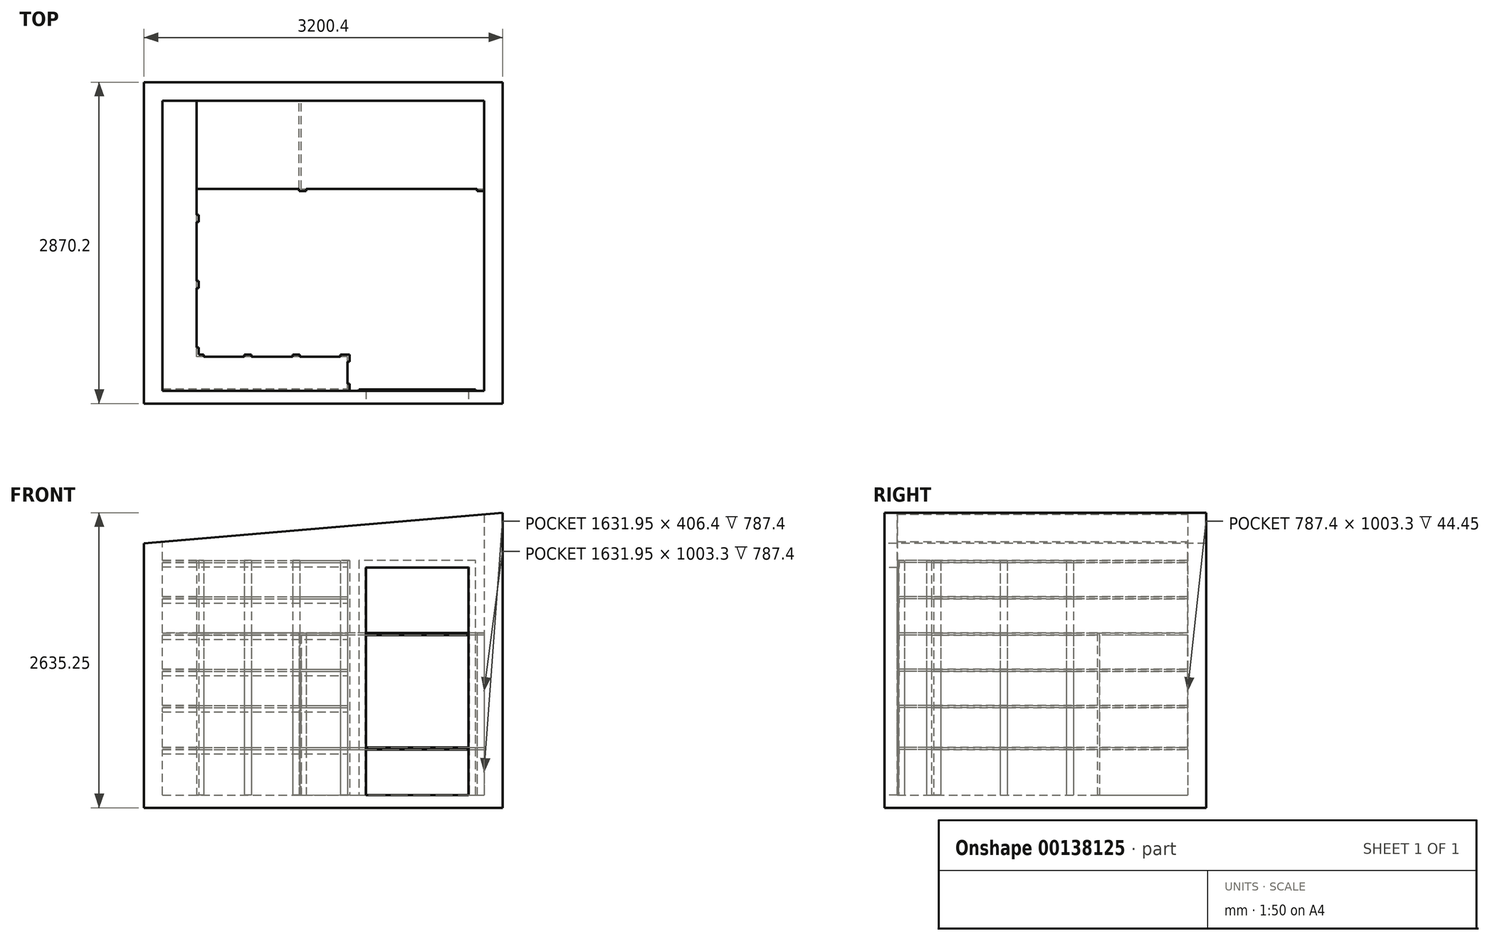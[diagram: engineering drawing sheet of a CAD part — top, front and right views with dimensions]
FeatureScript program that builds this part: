
annotation { "Feature Type Name" : "Feature", "Feature Type Description" : "" }
export const myFeature = defineFeature(function(context is Context, id is Id, definition is map)
    precondition{}
    {
        {
            var Q0;
            Q0=qCreatedBy(makeId("Right.planeOp"),FACE);
            var sketch = newSketch(context, id + "F0", { "sketchPlane" : qUnion([Q0])});
            skLineSegment(sketch, "E0.bottom", {"start": v(0, 0) * mm, "end": v(2590.8, 0) * mm});
            skLineSegment(sketch, "E0.top", {"start": v(0, 2520.95) * mm, "end": v(2590.8, 2520.95) * mm});
            skLineSegment(sketch, "E0.left", {"start": v(0, 0) * mm, "end": v(0, 2520.95) * mm});
            skLineSegment(sketch, "E0.right", {"start": v(2590.8, 0) * mm, "end": v(2590.8, 2520.95) * mm});
            skSolve(sketch);
        }
        {
            var Q0;
            Q0 = qSketchRegion(id + "F0", true);
            extrude(context, id + "F1", {"entities" : qUnion([Q0]), "depth" : 165.1 * mm});
        }
        {
            var Q0;
            Q0=makeQuery(id+"F1.opExtrude","SWEPT_FACE",FACE,{"disambiguationData":[OSD([sQuery(id+"F0.wireOp",EDGE,"E0.left")])]});
            var sketch = newSketch(context, id + "F2", { "sketchPlane" : qUnion([Q0])});
            skLineSegment(sketch, "E1.bottom", {"start": v(0, 2520.95) * mm, "end": v(3035.3, 2520.95) * mm});
            skLineSegment(sketch, "E1.top", {"start": v(0, 0) * mm, "end": v(3035.3, 0) * mm});
            skLineSegment(sketch, "E1.left", {"start": v(0, 2520.95) * mm, "end": v(0, 0) * mm});
            skLineSegment(sketch, "E1.right", {"start": v(3035.3, 2520.95) * mm, "end": v(3035.3, 0) * mm});
            skSolve(sketch);
        }
        {
            var Q0;
            Q0 = qSketchRegion(id + "F2", true);
            extrude(context, id + "F3", {"entities" : qUnion([Q0]), "operationType" : NewBodyOperationType.ADD, "depth" : 114.3 * mm});
        }
        {
            var Q0;
            Q0=makeQuery(id+"F1.opExtrude","SWEPT_FACE",FACE,{"disambiguationData":[OSD([sQuery(id+"F0.wireOp",EDGE,"E0.right")])]});
            var sketch = newSketch(context, id + "F4", { "sketchPlane" : qUnion([Q0])});
            skLineSegment(sketch, "E2.bottom", {"start": v(0, 2520.95) * mm, "end": v(-3035.3, 2520.95) * mm});
            skLineSegment(sketch, "E2.top", {"start": v(0, 0) * mm, "end": v(-3035.3, 0) * mm});
            skLineSegment(sketch, "E2.left", {"start": v(0, 2520.95) * mm, "end": v(0, 0) * mm});
            skLineSegment(sketch, "E2.right", {"start": v(-3035.3, 2520.95) * mm, "end": v(-3035.3, 0) * mm});
            skSolve(sketch);
        }
        {
            var Q0;
            Q0 = qSketchRegion(id + "F4", true);
            extrude(context, id + "F5", {"entities" : qUnion([Q0]), "operationType" : NewBodyOperationType.ADD, "depth" : 165.1 * mm});
        }
        {
            var Q0;
            Q0=makeQuery(id+"F3.opExtrude","SWEPT_FACE",FACE,{"disambiguationData":[OSD([sQuery(id+"F2.wireOp",EDGE,"E1.right")])]});
            var sketch = newSketch(context, id + "F6", { "sketchPlane" : qUnion([Q0])});
            skLineSegment(sketch, "E3.bottom", {"start": v(-114.3, 2520.95) * mm, "end": v(2755.9, 2520.95) * mm});
            skLineSegment(sketch, "E3.top", {"start": v(-114.3, 0) * mm, "end": v(2755.9, 0) * mm});
            skLineSegment(sketch, "E3.left", {"start": v(-114.3, 2520.95) * mm, "end": v(-114.3, 0) * mm});
            skLineSegment(sketch, "E3.right", {"start": v(2755.9, 2520.95) * mm, "end": v(2755.9, 0) * mm});
            skSolve(sketch);
        }
        {
            var Q0;
            Q0 = qSketchRegion(id + "F6", true);
            extrude(context, id + "F7", {"entities" : qUnion([Q0]), "operationType" : NewBodyOperationType.ADD, "depth" : 165.1 * mm});
        }
        {
            var Q0;
            Q0=makeQuery(id+"F7.boolean.opBoolean","MERGE",FACE,{"derivedFrom":[makeQuery(id+"F3.opExtrude","CAP_FACE",FACE,{"disambiguationData":[OSD([sQuery(id+"F2.wireOp",EDGE,"E1.bottom"),sQuery(id+"F2.wireOp",EDGE,"E1.top"),sQuery(id+"F2.wireOp",EDGE,"E1.left"),sQuery(id+"F2.wireOp",EDGE,"E1.right")])],"isStart":false}),makeQuery(id+"F7.opExtrude","SWEPT_FACE",FACE,{"disambiguationData":[OSD([sQuery(id+"F6.wireOp",EDGE,"E3.left")])]})]});
            var sketch = newSketch(context, id + "F8", { "sketchPlane" : qUnion([Q0])});
            skLineSegment(sketch, "E4.bottom", {"start": v(2895.6, 0) * mm, "end": v(1981.2, 0) * mm});
            skLineSegment(sketch, "E4.top", {"start": v(2895.6, 2032) * mm, "end": v(1981.2, 2032) * mm});
            skLineSegment(sketch, "E4.left", {"start": v(2895.6, 0) * mm, "end": v(2895.6, 2032) * mm});
            skLineSegment(sketch, "E4.right", {"start": v(1981.2, 0) * mm, "end": v(1981.2, 2032) * mm});
            skSolve(sketch);
        }
        {
            var Q0;
            Q0=makeQuery(id+"F8.imprint","IMPRINT",FACE,{"disambiguationData":[TD([[makeQuery(id+"F8.imprint","IMPRINT",EDGE,{"derivedFrom":sQuery(id+"F8.wireOp",EDGE,"E4.top")}),-1.0]])]});
            var sketch = newSketch(context, id + "F9", { "sketchPlane" : qUnion([Q0])});
            skLineSegment(sketch, "E5", {"start": v(0, 2247.9) * mm, "end": v(3200.4, 2520.95) * mm});
            skLineSegment(sketch, "E6", {"start": v(3200.4, 2520.95) * mm, "end": v(0, 2520.95) * mm});
            skLineSegment(sketch, "E7", {"start": v(0, 2520.95) * mm, "end": v(0, 2247.9) * mm});
            skSolve(sketch);
        }
        {
            var Q0;
            Q0 = qSketchRegion(id + "F9", true);
            extrude(context, id + "F10", {"entities" : qUnion([Q0]), "operationType" : NewBodyOperationType.REMOVE, "endBound" : BoundingType.THROUGH_ALL, "oppositeDirection" : true, "depth" : 25.4 * mm});
        }
        {
            var Q0;
            Q0 = qSketchRegion(id + "F8", true);
            extrude(context, id + "F11", {"entities" : qUnion([Q0]), "operationType" : NewBodyOperationType.REMOVE, "oppositeDirection" : true, "depth" : 114.3 * mm});
        }
        {
            var Q0;
            Q0=makeQuery(id+"F7.boolean.opBoolean","MERGE",FACE,{"derivedFrom":[makeQuery(id+"F5.boolean.opBoolean","MERGE",FACE,{"derivedFrom":[makeQuery(id+"F3.boolean.opBoolean","MERGE",FACE,{"derivedFrom":[makeQuery(id+"F1.opExtrude","SWEPT_FACE",FACE,{"disambiguationData":[OSD([sQuery(id+"F0.wireOp",EDGE,"E0.bottom")])]}),makeQuery(id+"F3.opExtrude","SWEPT_FACE",FACE,{"disambiguationData":[OSD([sQuery(id+"F2.wireOp",EDGE,"E1.top")])]})]}),makeQuery(id+"F5.opExtrude","SWEPT_FACE",FACE,{"disambiguationData":[OSD([sQuery(id+"F4.wireOp",EDGE,"E2.top")])]})]}),makeQuery(id+"F7.opExtrude","SWEPT_FACE",FACE,{"disambiguationData":[OSD([sQuery(id+"F6.wireOp",EDGE,"E3.top")])]})]});
            var sketch = newSketch(context, id + "F12", { "sketchPlane" : qUnion([Q0])});
            skLineSegment(sketch, "E8.bottom", {"start": v(0, 114.3) * mm, "end": v(3200.4, 114.3) * mm});
            skLineSegment(sketch, "E8.top", {"start": v(0, -2755.9) * mm, "end": v(3200.4, -2755.9) * mm});
            skLineSegment(sketch, "E8.left", {"start": v(0, 114.3) * mm, "end": v(0, -2755.9) * mm});
            skLineSegment(sketch, "E8.right", {"start": v(3200.4, 114.3) * mm, "end": v(3200.4, -2755.9) * mm});
            skSolve(sketch);
        }
        {
            var Q0;
            Q0 = qSketchRegion(id + "F12", true);
            extrude(context, id + "F13", {"entities" : qUnion([Q0]), "operationType" : NewBodyOperationType.ADD, "depth" : 114.3 * mm});
        }
        {
            var Q0;
            Q0=makeQuery(id+"F3.opExtrude","CAP_FACE",FACE,{"disambiguationData":[OSD([sQuery(id+"F2.wireOp",EDGE,"E1.bottom"),sQuery(id+"F2.wireOp",EDGE,"E1.top"),sQuery(id+"F2.wireOp",EDGE,"E1.left"),sQuery(id+"F2.wireOp",EDGE,"E1.right")])],"isStart":true});
            var sketch = newSketch(context, id + "F14", { "sketchPlane" : qUnion([Q0])});
            skLineSegment(sketch, "E9", {"start": v(-1974.85, 0) * mm, "end": v(-1974.85, 2038.35) * mm});
            skLineSegment(sketch, "E10", {"start": v(-1974.85, 2038.35) * mm, "end": v(-2901.95, 2038.35) * mm});
            skLineSegment(sketch, "E11", {"start": v(-2901.95, 2038.35) * mm, "end": v(-2901.95, 0) * mm});
            skPoint(sketch, "E11.endSnap0", {"position": v(-2965.45, 0) * mm});
            skLineSegment(sketch, "E12", {"start": v(-2901.95, 0) * mm, "end": v(-2959.1, 0) * mm});
            skLineSegment(sketch, "E13", {"start": v(-2959.1, 0) * mm, "end": v(-2959.1, 2095.5) * mm});
            skLineSegment(sketch, "E14", {"start": v(-2959.1, 2095.5) * mm, "end": v(-1917.7, 2095.5) * mm});
            skLineSegment(sketch, "E15", {"start": v(-1917.7, 2095.5) * mm, "end": v(-1917.7, 0) * mm});
            skLineSegment(sketch, "E16", {"start": v(-1917.7, 0) * mm, "end": v(-1974.85, 0) * mm});
            skSolve(sketch);
        }
        {
            var Q0;
            Q0 = qSketchRegion(id + "F14", true);
            extrude(context, id + "F15", {"entities" : qUnion([Q0]), "operationType" : NewBodyOperationType.ADD, "depth" : 12.7 * mm});
        }
        {
            var Q0;
            Q0=makeQuery(id+"F15.boolean.opBoolean","SPLIT",FACE,{"disambiguationData":[TD([makeQuery(id+"F10.boolean.opBoolean","COPY",FACE,{"derivedFrom":makeQuery(id+"F10.opExtrude","SWEPT_FACE",FACE,{"disambiguationData":[OSD([sQuery(id+"F9.wireOp",EDGE,"E5")])]})})])],"derivedFrom":makeQuery(id+"F3.opExtrude","CAP_FACE",FACE,{"disambiguationData":[OSD([sQuery(id+"F2.wireOp",EDGE,"E1.bottom"),sQuery(id+"F2.wireOp",EDGE,"E1.top"),sQuery(id+"F2.wireOp",EDGE,"E1.left"),sQuery(id+"F2.wireOp",EDGE,"E1.right")])],"isStart":true})});
            var Q1;
            Q1=makeQuery(id+"F13.boolean.opBoolean","MERGE",FACE,{"derivedFrom":[makeQuery(id+"F7.boolean.opBoolean","MERGE",FACE,{"derivedFrom":[makeQuery(id+"F3.opExtrude","CAP_FACE",FACE,{"disambiguationData":[OSD([sQuery(id+"F2.wireOp",EDGE,"E1.bottom"),sQuery(id+"F2.wireOp",EDGE,"E1.top"),sQuery(id+"F2.wireOp",EDGE,"E1.left"),sQuery(id+"F2.wireOp",EDGE,"E1.right")])],"isStart":false}),makeQuery(id+"F7.opExtrude","SWEPT_FACE",FACE,{"disambiguationData":[OSD([sQuery(id+"F6.wireOp",EDGE,"E3.left")])]})]}),makeQuery(id+"F13.opExtrude","SWEPT_FACE",FACE,{"disambiguationData":[OSD([sQuery(id+"F12.wireOp",EDGE,"E8.bottom")])]})]});
            cPlane(context, id + "F16", {"entities" : qUnion([Q0, Q1]), "cplaneType" : CPlaneType.MID_PLANE, "offset" : 25.4 * mm, "width" : 152.4 * mm, "height" : 152.4 * mm});
        }
        {
            var Q0;
            Q0=makeQuery(id+"F13.opExtrude","CAP_FACE",FACE,{"disambiguationData":[OSD([sQuery(id+"F12.wireOp",EDGE,"E8.bottom"),sQuery(id+"F12.wireOp",EDGE,"E8.top"),sQuery(id+"F12.wireOp",EDGE,"E8.left"),sQuery(id+"F12.wireOp",EDGE,"E8.right")])],"isStart":true});
            var sketch = newSketch(context, id + "F17", { "sketchPlane" : qUnion([Q0])});
            skLineSegment(sketch, "E17.bottom", {"start": v(3200.4, 304.8) * mm, "end": v(469.9, 304.8) * mm});
            skLineSegment(sketch, "E17.top", {"start": v(3200.4, 2755.9) * mm, "end": v(469.9, 2755.9) * mm});
            skLineSegment(sketch, "E17.left", {"start": v(3200.4, 304.8) * mm, "end": v(3200.4, 2755.9) * mm});
            skLineSegment(sketch, "E17.right", {"start": v(469.9, 304.8) * mm, "end": v(469.9, 2755.9) * mm});
            skSolve(sketch);
        }
        {
            var Q0;
            Q0=makeQuery(id+"F15.boolean.opBoolean","SPLIT",FACE,{"disambiguationData":[TD([makeQuery(id+"F10.boolean.opBoolean","COPY",FACE,{"derivedFrom":makeQuery(id+"F10.opExtrude","SWEPT_FACE",FACE,{"disambiguationData":[OSD([sQuery(id+"F9.wireOp",EDGE,"E5")])]})})])],"derivedFrom":makeQuery(id+"F3.opExtrude","CAP_FACE",FACE,{"disambiguationData":[OSD([sQuery(id+"F2.wireOp",EDGE,"E1.bottom"),sQuery(id+"F2.wireOp",EDGE,"E1.top"),sQuery(id+"F2.wireOp",EDGE,"E1.left"),sQuery(id+"F2.wireOp",EDGE,"E1.right")])],"isStart":true})});
            var sketch = newSketch(context, id + "F18", { "sketchPlane" : qUnion([Q0])});
            skLineSegment(sketch, "E18.bottom", {"start": v(-165.1, 406.4) * mm, "end": v(-1816.1, 406.4) * mm});
            skLineSegment(sketch, "E18.top", {"start": v(-165.1, 425.45) * mm, "end": v(-1816.1, 425.45) * mm});
            skLineSegment(sketch, "E18.left", {"start": v(-165.1, 406.4) * mm, "end": v(-165.1, 425.45) * mm});
            skLineSegment(sketch, "E18.right", {"start": v(-1816.1, 406.4) * mm, "end": v(-1816.1, 425.45) * mm});
            skLineSegment(sketch, "E19.bottom", {"start": v(-165.1, 781.05) * mm, "end": v(-1816.1, 781.05) * mm});
            skLineSegment(sketch, "E19.top", {"start": v(-165.1, 800.1) * mm, "end": v(-1816.1, 800.1) * mm});
            skLineSegment(sketch, "E19.left", {"start": v(-165.1, 781.05) * mm, "end": v(-165.1, 800.1) * mm});
            skLineSegment(sketch, "E19.right", {"start": v(-1816.1, 781.05) * mm, "end": v(-1816.1, 800.1) * mm});
            skLineSegment(sketch, "E20.bottom", {"start": v(-165.1, 1104.9) * mm, "end": v(-1816.1, 1104.9) * mm});
            skLineSegment(sketch, "E20.top", {"start": v(-165.1, 1123.95) * mm, "end": v(-1816.1, 1123.95) * mm});
            skLineSegment(sketch, "E20.left", {"start": v(-165.1, 1104.9) * mm, "end": v(-165.1, 1123.95) * mm});
            skLineSegment(sketch, "E20.right", {"start": v(-1816.1, 1104.9) * mm, "end": v(-1816.1, 1123.95) * mm});
            skLineSegment(sketch, "E21.bottom", {"start": v(-165.1, 1428.75) * mm, "end": v(-1816.1, 1428.75) * mm});
            skLineSegment(sketch, "E21.top", {"start": v(-165.1, 1447.8) * mm, "end": v(-1816.1, 1447.8) * mm});
            skLineSegment(sketch, "E21.left", {"start": v(-165.1, 1428.75) * mm, "end": v(-165.1, 1447.8) * mm});
            skLineSegment(sketch, "E21.right", {"start": v(-1816.1, 1428.75) * mm, "end": v(-1816.1, 1447.8) * mm});
            skLineSegment(sketch, "E22.bottom", {"start": v(-165.1, 1752.6) * mm, "end": v(-1816.1, 1752.6) * mm});
            skLineSegment(sketch, "E22.top", {"start": v(-165.1, 1771.65) * mm, "end": v(-1816.1, 1771.65) * mm});
            skLineSegment(sketch, "E22.left", {"start": v(-165.1, 1752.6) * mm, "end": v(-165.1, 1771.65) * mm});
            skLineSegment(sketch, "E22.right", {"start": v(-1816.1, 1752.6) * mm, "end": v(-1816.1, 1771.65) * mm});
            skLineSegment(sketch, "E23.bottom", {"start": v(-165.1, 2076.45) * mm, "end": v(-1816.1, 2076.45) * mm});
            skLineSegment(sketch, "E23.top", {"start": v(-165.1, 2095.5) * mm, "end": v(-1816.1, 2095.5) * mm});
            skLineSegment(sketch, "E23.left", {"start": v(-165.1, 2076.45) * mm, "end": v(-165.1, 2095.5) * mm});
            skLineSegment(sketch, "E23.right", {"start": v(-1816.1, 2076.45) * mm, "end": v(-1816.1, 2095.5) * mm});
            skSolve(sketch);
        }
        {
            var Q0;
            Q0 = qSketchRegion(id + "F18", true);
            extrude(context, id + "F19", {"entities" : qUnion([Q0]), "operationType" : NewBodyOperationType.ADD, "depth" : 304.8 * mm});
        }
        {
            var Q0;
            Q0=makeQuery(id+"F15.boolean.opBoolean","SPLIT",FACE,{"disambiguationData":[TD([makeQuery(id+"F10.boolean.opBoolean","COPY",FACE,{"derivedFrom":makeQuery(id+"F10.opExtrude","SWEPT_FACE",FACE,{"disambiguationData":[OSD([sQuery(id+"F9.wireOp",EDGE,"E5")])]})})])],"derivedFrom":makeQuery(id+"F3.opExtrude","CAP_FACE",FACE,{"disambiguationData":[OSD([sQuery(id+"F2.wireOp",EDGE,"E1.bottom"),sQuery(id+"F2.wireOp",EDGE,"E1.top"),sQuery(id+"F2.wireOp",EDGE,"E1.left"),sQuery(id+"F2.wireOp",EDGE,"E1.right")])],"isStart":true})});
            var sketch = newSketch(context, id + "F20", { "sketchPlane" : qUnion([Q0])});
            skLineSegment(sketch, "E24.bottom", {"start": v(-165.1, 2076.45) * mm, "end": v(-1816.1, 2076.45) * mm});
            skLineSegment(sketch, "E24.top", {"start": v(-165.1, 2038.35) * mm, "end": v(-1816.1, 2038.35) * mm});
            skLineSegment(sketch, "E24.left", {"start": v(-165.1, 2076.45) * mm, "end": v(-165.1, 2038.35) * mm});
            skLineSegment(sketch, "E24.right", {"start": v(-1816.1, 2076.45) * mm, "end": v(-1816.1, 2038.35) * mm});
            skLineSegment(sketch, "E25.bottom", {"start": v(-165.1, 1752.6) * mm, "end": v(-1816.1, 1752.6) * mm});
            skLineSegment(sketch, "E25.top", {"start": v(-165.1, 1714.5) * mm, "end": v(-1816.1, 1714.5) * mm});
            skLineSegment(sketch, "E25.left", {"start": v(-165.1, 1752.6) * mm, "end": v(-165.1, 1714.5) * mm});
            skLineSegment(sketch, "E25.right", {"start": v(-1816.1, 1752.6) * mm, "end": v(-1816.1, 1714.5) * mm});
            skLineSegment(sketch, "E26.bottom", {"start": v(-165.1, 1428.75) * mm, "end": v(-1816.1, 1428.75) * mm});
            skLineSegment(sketch, "E26.top", {"start": v(-165.1, 1390.65) * mm, "end": v(-1816.1, 1390.65) * mm});
            skLineSegment(sketch, "E26.left", {"start": v(-165.1, 1428.75) * mm, "end": v(-165.1, 1390.65) * mm});
            skLineSegment(sketch, "E26.right", {"start": v(-1816.1, 1428.75) * mm, "end": v(-1816.1, 1390.65) * mm});
            skLineSegment(sketch, "E27.bottom", {"start": v(-165.1, 1104.9) * mm, "end": v(-1816.1, 1104.9) * mm});
            skLineSegment(sketch, "E27.top", {"start": v(-165.1, 1066.8) * mm, "end": v(-1816.1, 1066.8) * mm});
            skLineSegment(sketch, "E27.left", {"start": v(-165.1, 1104.9) * mm, "end": v(-165.1, 1066.8) * mm});
            skLineSegment(sketch, "E27.right", {"start": v(-1816.1, 1104.9) * mm, "end": v(-1816.1, 1066.8) * mm});
            skLineSegment(sketch, "E28.bottom", {"start": v(-165.1, 406.4) * mm, "end": v(-1816.1, 406.4) * mm});
            skLineSegment(sketch, "E28.top", {"start": v(-165.1, 368.3) * mm, "end": v(-1816.1, 368.3) * mm});
            skLineSegment(sketch, "E28.left", {"start": v(-165.1, 406.4) * mm, "end": v(-165.1, 368.3) * mm});
            skLineSegment(sketch, "E28.right", {"start": v(-1816.1, 406.4) * mm, "end": v(-1816.1, 368.3) * mm});
            skLineSegment(sketch, "E29.bottom", {"start": v(-165.1, 781.05) * mm, "end": v(-1816.1, 781.05) * mm});
            skLineSegment(sketch, "E29.top", {"start": v(-165.1, 742.95) * mm, "end": v(-1816.1, 742.95) * mm});
            skLineSegment(sketch, "E29.left", {"start": v(-165.1, 781.05) * mm, "end": v(-165.1, 742.95) * mm});
            skLineSegment(sketch, "E29.right", {"start": v(-1816.1, 781.05) * mm, "end": v(-1816.1, 742.95) * mm});
            skSolve(sketch);
        }
        {
            var Q0;
            Q0 = qSketchRegion(id + "F20", true);
            extrude(context, id + "F21", {"entities" : qUnion([Q0]), "operationType" : NewBodyOperationType.ADD, "depth" : 19.05 * mm});
        }
        {
            var Q0;
            Q0=makeQuery(id+"Fllte4z2JdaSj08_1.boolean.opBoolean","MERGE",FACE,{"derivedFrom":[makeQuery(id+"F13.opExtrude","CAP_FACE",FACE,{"disambiguationData":[OSD([sQuery(id+"F12.wireOp",EDGE,"E8.bottom"),sQuery(id+"F12.wireOp",EDGE,"E8.top"),sQuery(id+"F12.wireOp",EDGE,"E8.left"),sQuery(id+"F12.wireOp",EDGE,"E8.right")])],"isStart":true}),makeQuery(id+"Fllte4z2JdaSj08_1.opExtrude","CAP_FACE",FACE,{"disambiguationData":[OSD([sQuery(id+"F17.wireOp",EDGE,"E17.bottom"),sQuery(id+"F17.wireOp",EDGE,"E17.top"),sQuery(id+"F17.wireOp",EDGE,"E17.left"),sQuery(id+"F17.wireOp",EDGE,"E17.right")])],"isStart":true})]});
            var sketch = newSketch(context, id + "F22", { "sketchPlane" : qUnion([Q0])});
            skLineSegment(sketch, "E30.bottom", {"start": v(1835.15, 0) * mm, "end": v(1816.1, 0) * mm});
            skLineSegment(sketch, "E30.top", {"start": v(1835.15, 63.5) * mm, "end": v(1816.1, 63.5) * mm});
            skLineSegment(sketch, "E30.left", {"start": v(1835.15, 0) * mm, "end": v(1835.15, 63.5) * mm});
            skLineSegment(sketch, "E30.right", {"start": v(1816.1, 0) * mm, "end": v(1816.1, 63.5) * mm});
            skLineSegment(sketch, "E31.bottom", {"start": v(1835.15, 260.35) * mm, "end": v(1816.1, 260.35) * mm});
            skLineSegment(sketch, "E31.top", {"start": v(1835.15, 323.85) * mm, "end": v(1816.1, 323.85) * mm});
            skLineSegment(sketch, "E31.left", {"start": v(1835.15, 260.35) * mm, "end": v(1835.15, 323.85) * mm});
            skLineSegment(sketch, "E31.right", {"start": v(1816.1, 260.35) * mm, "end": v(1816.1, 323.85) * mm});
            skLineSegment(sketch, "E32.bottom", {"start": v(1816.1, 323.85) * mm, "end": v(1752.6, 323.85) * mm});
            skLineSegment(sketch, "E32.top", {"start": v(1816.1, 304.8) * mm, "end": v(1752.6, 304.8) * mm});
            skLineSegment(sketch, "E32.left", {"start": v(1816.1, 323.85) * mm, "end": v(1816.1, 304.8) * mm});
            skLineSegment(sketch, "E32.right", {"start": v(1752.6, 323.85) * mm, "end": v(1752.6, 304.8) * mm});
            skLineSegment(sketch, "E33.bottom", {"start": v(1390.65, 323.85) * mm, "end": v(1327.15, 323.85) * mm});
            skLineSegment(sketch, "E33.top", {"start": v(1390.65, 304.8) * mm, "end": v(1327.15, 304.8) * mm});
            skLineSegment(sketch, "E33.left", {"start": v(1390.65, 323.85) * mm, "end": v(1390.65, 304.8) * mm});
            skLineSegment(sketch, "E33.right", {"start": v(1327.15, 323.85) * mm, "end": v(1327.15, 304.8) * mm});
            skLineSegment(sketch, "E34.bottom", {"start": v(533.4, 323.85) * mm, "end": v(469.9, 323.85) * mm});
            skLineSegment(sketch, "E34.top", {"start": v(533.4, 304.8) * mm, "end": v(469.9, 304.8) * mm});
            skLineSegment(sketch, "E34.left", {"start": v(533.4, 323.85) * mm, "end": v(533.4, 304.8) * mm});
            skLineSegment(sketch, "E34.right", {"start": v(469.9, 323.85) * mm, "end": v(469.9, 304.8) * mm});
            skLineSegment(sketch, "E35.bottom", {"start": v(469.9, 323.85) * mm, "end": v(488.95, 323.85) * mm});
            skLineSegment(sketch, "E35.top", {"start": v(469.9, 387.35) * mm, "end": v(488.95, 387.35) * mm});
            skLineSegment(sketch, "E35.left", {"start": v(469.9, 323.85) * mm, "end": v(469.9, 387.35) * mm});
            skLineSegment(sketch, "E35.right", {"start": v(488.95, 323.85) * mm, "end": v(488.95, 387.35) * mm});
            skLineSegment(sketch, "E36.bottom", {"start": v(469.9, 917.57) * mm, "end": v(488.95, 917.57) * mm});
            skLineSegment(sketch, "E36.top", {"start": v(469.9, 981.07) * mm, "end": v(488.95, 981.07) * mm});
            skLineSegment(sketch, "E36.left", {"start": v(469.9, 917.57) * mm, "end": v(469.9, 981.07) * mm});
            skLineSegment(sketch, "E36.right", {"start": v(488.95, 917.57) * mm, "end": v(488.95, 981.07) * mm});
            skLineSegment(sketch, "E37.bottom", {"start": v(469.9, 1508.13) * mm, "end": v(488.95, 1508.13) * mm});
            skLineSegment(sketch, "E37.top", {"start": v(469.9, 1571.62) * mm, "end": v(488.95, 1571.62) * mm});
            skLineSegment(sketch, "E37.left", {"start": v(469.9, 1508.13) * mm, "end": v(469.9, 1571.62) * mm});
            skLineSegment(sketch, "E37.right", {"start": v(488.95, 1508.13) * mm, "end": v(488.95, 1571.62) * mm});
            skLineSegment(sketch, "E38.bottom", {"start": v(958.85, 304.8) * mm, "end": v(895.35, 304.8) * mm});
            skLineSegment(sketch, "E38.top", {"start": v(958.85, 323.85) * mm, "end": v(895.35, 323.85) * mm});
            skLineSegment(sketch, "E38.left", {"start": v(958.85, 304.8) * mm, "end": v(958.85, 323.85) * mm});
            skLineSegment(sketch, "E38.right", {"start": v(895.35, 304.8) * mm, "end": v(895.35, 323.85) * mm});
            skSolve(sketch);
        }
        {
            var Q0;
            Q0 = qSketchRegion(id + "F22", true);
            extrude(context, id + "F23", {"entities" : qUnion([Q0]), "operationType" : NewBodyOperationType.ADD, "depth" : 2095.5 * mm});
        }
        {
            var Q0;
            Q0=makeQuery(id+"F1.opExtrude","CAP_FACE",FACE,{"disambiguationData":[OSD([sQuery(id+"F0.wireOp",EDGE,"E0.bottom"),sQuery(id+"F0.wireOp",EDGE,"E0.top"),sQuery(id+"F0.wireOp",EDGE,"E0.left"),sQuery(id+"F0.wireOp",EDGE,"E0.right")])],"isStart":false});
            var sketch = newSketch(context, id + "F24", { "sketchPlane" : qUnion([Q0])});
            skPoint(sketch, "E39.oppositeSnap0", {"position": v(161.93, 2076.45) * mm});
            skLineSegment(sketch, "E39.bottom", {"start": v(304.8, 2095.5) * mm, "end": v(2590.8, 2095.5) * mm});
            skLineSegment(sketch, "E39.top", {"start": v(304.8, 2076.45) * mm, "end": v(2590.8, 2076.45) * mm});
            skLineSegment(sketch, "E39.left", {"start": v(304.8, 2095.5) * mm, "end": v(304.8, 2076.45) * mm});
            skLineSegment(sketch, "E39.right", {"start": v(2590.8, 2095.5) * mm, "end": v(2590.8, 2076.45) * mm});
            skLineSegment(sketch, "E40.bottom", {"start": v(304.8, 1771.65) * mm, "end": v(2590.8, 1771.65) * mm});
            skLineSegment(sketch, "E40.top", {"start": v(304.8, 1752.6) * mm, "end": v(2590.8, 1752.6) * mm});
            skLineSegment(sketch, "E40.left", {"start": v(304.8, 1771.65) * mm, "end": v(304.8, 1752.6) * mm});
            skLineSegment(sketch, "E40.right", {"start": v(2590.8, 1771.65) * mm, "end": v(2590.8, 1752.6) * mm});
            skLineSegment(sketch, "E41.bottom", {"start": v(304.8, 1447.8) * mm, "end": v(2590.8, 1447.8) * mm});
            skLineSegment(sketch, "E41.top", {"start": v(304.8, 1428.75) * mm, "end": v(2590.8, 1428.75) * mm});
            skLineSegment(sketch, "E41.left", {"start": v(304.8, 1447.8) * mm, "end": v(304.8, 1428.75) * mm});
            skLineSegment(sketch, "E41.right", {"start": v(2590.8, 1447.8) * mm, "end": v(2590.8, 1428.75) * mm});
            skLineSegment(sketch, "E42.bottom", {"start": v(304.8, 425.45) * mm, "end": v(2590.8, 425.45) * mm});
            skLineSegment(sketch, "E42.top", {"start": v(304.8, 406.4) * mm, "end": v(2590.8, 406.4) * mm});
            skLineSegment(sketch, "E42.left", {"start": v(304.8, 425.45) * mm, "end": v(304.8, 406.4) * mm});
            skLineSegment(sketch, "E42.right", {"start": v(2590.8, 425.45) * mm, "end": v(2590.8, 406.4) * mm});
            skLineSegment(sketch, "E43.bottom", {"start": v(304.8, 800.1) * mm, "end": v(2590.8, 800.1) * mm});
            skLineSegment(sketch, "E43.top", {"start": v(304.8, 781.05) * mm, "end": v(2590.8, 781.05) * mm});
            skLineSegment(sketch, "E43.left", {"start": v(304.8, 800.1) * mm, "end": v(304.8, 781.05) * mm});
            skLineSegment(sketch, "E43.right", {"start": v(2590.8, 800.1) * mm, "end": v(2590.8, 781.05) * mm});
            skLineSegment(sketch, "E44.bottom", {"start": v(304.8, 1123.95) * mm, "end": v(2590.8, 1123.95) * mm});
            skLineSegment(sketch, "E44.top", {"start": v(304.8, 1104.9) * mm, "end": v(2590.8, 1104.9) * mm});
            skLineSegment(sketch, "E44.left", {"start": v(304.8, 1123.95) * mm, "end": v(304.8, 1104.9) * mm});
            skLineSegment(sketch, "E44.right", {"start": v(2590.8, 1123.95) * mm, "end": v(2590.8, 1104.9) * mm});
            skSolve(sketch);
        }
        {
            var Q0;
            Q0 = qSketchRegion(id + "F24", true);
            extrude(context, id + "F25", {"entities" : qUnion([Q0]), "operationType" : NewBodyOperationType.ADD, "depth" : 304.8 * mm});
        }
        {
            var Q0;
            Q0=makeQuery(id+"FbiakTUjsby0JHI_1.boolean.opBoolean","MERGE",FACE,{"derivedFrom":[makeQuery(id+"F25.boolean.opBoolean","MERGE",FACE,{"derivedFrom":[makeQuery(id+"F19.opExtrude","SWEPT_FACE",FACE,{"disambiguationData":[OSD([sQuery(id+"F18.wireOp",EDGE,"E18.top")])]}),makeQuery(id+"F25.opExtrude","SWEPT_FACE",FACE,{"disambiguationData":[OSD([sQuery(id+"F24.wireOp",EDGE,"E42.bottom")])]})]}),makeQuery(id+"FbiakTUjsby0JHI_1.opExtrude","SWEPT_FACE",FACE,{"disambiguationData":[OSD([sQuery(id+"FjrpZ5JBxR4FeDl_1.wireOp",EDGE,"Qz6daa4T-fzVh-TU3N-sVul-O9IAGAUrbKFN.bottom")])]})]});
            var sketch = newSketch(context, id + "F26", { "sketchPlane" : qUnion([Q0])});
            skLineSegment(sketch, "E45.bottom", {"start": v(622.3, 2590.8) * mm, "end": v(2044.7, 2590.8) * mm});
            skLineSegment(sketch, "E45.top", {"start": v(622.3, 1803.4) * mm, "end": v(2044.7, 1803.4) * mm});
            skLineSegment(sketch, "E45.left", {"start": v(622.3, 2590.8) * mm, "end": v(622.3, 1803.4) * mm});
            skLineSegment(sketch, "E45.right", {"start": v(2044.7, 2590.8) * mm, "end": v(2044.7, 1803.4) * mm});
            skLineSegment(sketch, "E46.bottom", {"start": v(2044.7, 2590.8) * mm, "end": v(3035.3, 2590.8) * mm});
            skLineSegment(sketch, "E46.top", {"start": v(2044.7, 1803.4) * mm, "end": v(3035.3, 1803.4) * mm});
            skLineSegment(sketch, "E46.right", {"start": v(3035.3, 2590.8) * mm, "end": v(3035.3, 1803.4) * mm});
            skSolve(sketch);
        }
        {
            var Q0;
            Q0 = qSketchRegion(id + "F26", true);
            extrude(context, id + "F27", {"entities" : qUnion([Q0]), "operationType" : NewBodyOperationType.REMOVE, "depth" : 990.6 * mm});
        }
        {
            var Q0;
            {var subQ0=sQuery(id+"F17.wireOp",EDGE,"E17.right");var subQ1=sQuery(id+"F17.wireOp",EDGE,"E17.bottom");var subQ2=makeQuery(id+"F17.imprint","INTERSECT",VERTEX,{"derivedFrom":[subQ1,subQ0]});Q0=makeQuery(id+"F17.imprint","IMPRINT",FACE,{"disambiguationData":[TD([[makeQuery(id+"F17.imprint","IMPRINT",EDGE,{"disambiguationData":[TD([[subQ2,1.0]])],"derivedFrom":subQ1}),-1.0]])]});}
            var sketch = newSketch(context, id + "F28", { "sketchPlane" : qUnion([Q0])});
            skLineSegment(sketch, "E47.bottom", {"start": v(1403.35, 1803.4) * mm, "end": v(1384.3, 1803.4) * mm});
            skLineSegment(sketch, "E47.top", {"start": v(1403.35, 2590.8) * mm, "end": v(1384.3, 2590.8) * mm});
            skLineSegment(sketch, "E47.left", {"start": v(1403.35, 1803.4) * mm, "end": v(1403.35, 2590.8) * mm});
            skLineSegment(sketch, "E47.right", {"start": v(1384.3, 1803.4) * mm, "end": v(1384.3, 2590.8) * mm});
            skLineSegment(sketch, "E48.bottom", {"start": v(1384.3, 1803.4) * mm, "end": v(1447.8, 1803.4) * mm});
            skLineSegment(sketch, "E48.top", {"start": v(1384.3, 1784.35) * mm, "end": v(1447.8, 1784.35) * mm});
            skLineSegment(sketch, "E48.left", {"start": v(1384.3, 1803.4) * mm, "end": v(1384.3, 1784.35) * mm});
            skLineSegment(sketch, "E48.right", {"start": v(1447.8, 1803.4) * mm, "end": v(1447.8, 1784.35) * mm});
            skLineSegment(sketch, "E49.bottom", {"start": v(2971.8, 1803.4) * mm, "end": v(3035.3, 1803.4) * mm});
            skLineSegment(sketch, "E49.top", {"start": v(2971.8, 1784.35) * mm, "end": v(3035.3, 1784.35) * mm});
            skLineSegment(sketch, "E49.left", {"start": v(2971.8, 1803.4) * mm, "end": v(2971.8, 1784.35) * mm});
            skLineSegment(sketch, "E49.right", {"start": v(3035.3, 1803.4) * mm, "end": v(3035.3, 1784.35) * mm});
            skSolve(sketch);
        }
        {
            var Q0;
            Q0 = qSketchRegion(id + "F28", true);
            extrude(context, id + "F29", {"entities" : qUnion([Q0]), "operationType" : NewBodyOperationType.ADD, "depth" : 1447.8 * mm});
        }
        {
            var Q0;
            Q0=makeQuery(id+"F29.opExtrude","CAP_FACE",FACE,{"disambiguationData":[OSD([sQuery(id+"F28.wireOp",EDGE,"E47.top"),sQuery(id+"F28.wireOp",EDGE,"E47.left"),sQuery(id+"F28.wireOp",EDGE,"E47.right"),sQuery(id+"F28.wireOp",EDGE,"E48.bottom"),sQuery(id+"F28.wireOp",EDGE,"E48.top"),sQuery(id+"F28.wireOp",EDGE,"E48.left"),sQuery(id+"F28.wireOp",EDGE,"E48.right")])],"isStart":false});
            var sketch = newSketch(context, id + "F30", { "sketchPlane" : qUnion([Q0])});
            skLineSegment(sketch, "E50.bottom", {"start": v(1384.3, 2590.8) * mm, "end": v(1403.35, 2590.8) * mm});
            skLineSegment(sketch, "E50.top", {"start": v(1384.3, 1803.4) * mm, "end": v(1403.35, 1803.4) * mm});
            skLineSegment(sketch, "E50.left", {"start": v(1384.3, 2590.8) * mm, "end": v(1384.3, 1803.4) * mm});
            skLineSegment(sketch, "E50.right", {"start": v(1403.35, 2590.8) * mm, "end": v(1403.35, 1803.4) * mm});
            skSolve(sketch);
        }
        {
            var Q0;
            Q0 = qSketchRegion(id + "F30", true);
            extrude(context, id + "F31", {"entities" : qUnion([Q0]), "operationType" : NewBodyOperationType.REMOVE, "oppositeDirection" : true, "depth" : 19.05 * mm});
        }
        {
            var Q0;
            Q0=makeQuery(id+"F31.boolean.opBoolean","COPY",FACE,{"derivedFrom":makeQuery(id+"F31.opExtrude","CAP_FACE",FACE,{"disambiguationData":[OSD([sQuery(id+"F30.wireOp",EDGE,"E50.bottom"),sQuery(id+"F30.wireOp",EDGE,"E50.top"),sQuery(id+"F30.wireOp",EDGE,"E50.left"),sQuery(id+"F30.wireOp",EDGE,"E50.right")])],"isStart":false})});
            var sketch = newSketch(context, id + "F32", { "sketchPlane" : qUnion([Q0])});
            skLineSegment(sketch, "E51.bottom", {"start": v(3035.3, 2590.8) * mm, "end": v(469.9, 2590.8) * mm});
            skLineSegment(sketch, "E51.top", {"start": v(3035.3, 1803.4) * mm, "end": v(469.9, 1803.4) * mm});
            skLineSegment(sketch, "E51.left", {"start": v(3035.3, 2590.8) * mm, "end": v(3035.3, 1803.4) * mm});
            skLineSegment(sketch, "E51.right", {"start": v(469.9, 2590.8) * mm, "end": v(469.9, 1803.4) * mm});
            skSolve(sketch);
        }
        {
            var Q0;
            Q0 = qSketchRegion(id + "F32", true);
            extrude(context, id + "F33", {"entities" : qUnion([Q0]), "operationType" : NewBodyOperationType.ADD, "depth" : 19.05 * mm});
        }
        {
            var Q0;
            Q0=makeQuery(id+"F33.boolean.opBoolean","SPLIT",FACE,{"disambiguationData":[TD([makeQuery(id+"F29.opExtrude","SWEPT_FACE",FACE,{"disambiguationData":[OSD([sQuery(id+"F28.wireOp",EDGE,"E47.left")])]})])],"derivedFrom":makeQuery(id+"F31.boolean.opBoolean","MERGE",FACE,{"derivedFrom":[makeQuery(id+"F5.opExtrude","CAP_FACE",FACE,{"disambiguationData":[OSD([sQuery(id+"F4.wireOp",EDGE,"E2.bottom"),sQuery(id+"F4.wireOp",EDGE,"E2.top"),sQuery(id+"F4.wireOp",EDGE,"E2.left"),sQuery(id+"F4.wireOp",EDGE,"E2.right")])],"isStart":true}),makeQuery(id+"F31.opExtrude","SWEPT_FACE",FACE,{"disambiguationData":[OSD([sQuery(id+"F30.wireOp",EDGE,"E50.bottom")])]})]})});
            var sketch = newSketch(context, id + "F34", { "sketchPlane" : qUnion([Q0])});
            skLineSegment(sketch, "E52.bottom", {"start": v(1403.35, 406.4) * mm, "end": v(3035.3, 406.4) * mm});
            skLineSegment(sketch, "E52.top", {"start": v(1403.35, 425.45) * mm, "end": v(3035.3, 425.45) * mm});
            skLineSegment(sketch, "E52.left", {"start": v(1403.35, 406.4) * mm, "end": v(1403.35, 425.45) * mm});
            skLineSegment(sketch, "E52.right", {"start": v(3035.3, 406.4) * mm, "end": v(3035.3, 425.45) * mm});
            skSolve(sketch);
        }
        {
            var Q0;
            Q0 = qSketchRegion(id + "F34", true);
            extrude(context, id + "F35", {"entities" : qUnion([Q0]), "operationType" : NewBodyOperationType.ADD, "depth" : 787.4 * mm});
        }
    });
